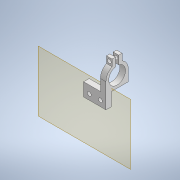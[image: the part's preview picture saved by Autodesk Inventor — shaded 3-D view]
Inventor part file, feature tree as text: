
AUTODESK INVENTOR PART (.ipt)
format: ipt  version: 2022 (Build 260153000, 153)  size: 158,720 bytes
history: native  units: mm
features: other x4, extrude x3, sketch x3, plane x1, reference x1, projected_geometry x1
ambient origin geometry x8: Origin, YZ Plane, XZ Plane, XY Plane, X Axis, Y Axis, Z Axis, Center Point
bodies: Solid1 (feature_tree)
feature tree (13):
  plane  "Work Plane1"
  extrude  "Extrusion1"  Depth=5.0mm
  extrude  "Extrusion2"  Depth=5.0mm
  extrude  "Extrusion3"  Depth=30.0mm
  sketch  "Sketch1"  dims[d0=5.0mm d1=5.0mm]
  reference  "Reference1"
  sketch  "Sketch2"  dims[d2=5.0mm d3=0.1mm]
  sketch  "Sketch3"  dims[d4=5.0mm d5=0.0mm d6=30.0mm d7=30.0mm d8=24.8mm d9=3.0mm d10=3.0mm d11=5.0mm d12=5.0mm d13=0.0mm d14=3.3mm d15=0.0mm d16=0.0mm]
  projected_geometry  "Projected Loop1"
  other  "<userpath>\OneDrive - Imperial College London\ROBOICP\Final Assembly\Final Assembly.iam"
  other  "Final Assembly.iam"
  other  "Solids Feeder Head Assembly:1"
  other  "body:1"
